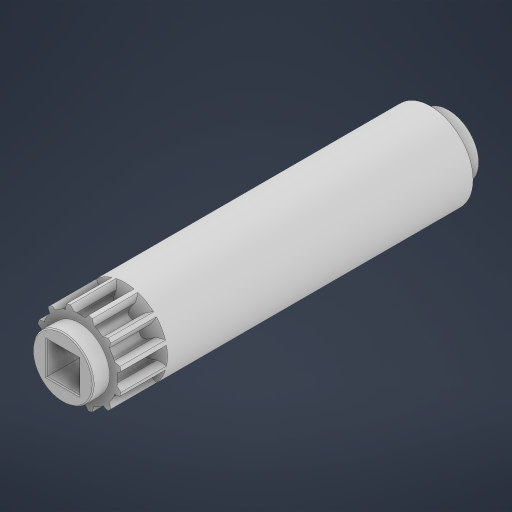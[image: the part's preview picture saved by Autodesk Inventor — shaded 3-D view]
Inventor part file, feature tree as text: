
AUTODESK INVENTOR PART (.ipt)
format: ipt  version: 2024.1 (Build 281209000, 209)  size: 670,208 bytes
history: native  units: in
note: dims shown in document units (in); Inventor stores cm internally (conversion verified against a paired STEP export)
features: extrude x10, sketch x7, projected_geometry x6, chamfer x5, reference x3, other x3, revolve x2, pattern_circular x1
ambient origin geometry x8: Origin, YZ Plane, XZ Plane, XY Plane, X Axis, Y Axis, Z Axis, Center Point
bodies: Solid1 (feature_tree)
feature tree (37):
  extrude  "Extrusion1"  TaperAngle=0.0deg  [1 undecoded]
  extrude  "Extrusion2"  Depth=4.7244in TaperAngle=360.0deg
  pattern_circular  "Circular Pattern1"  Angle=45.0deg  [1 undecoded]
  sketch  "Sketch2"  dims[d0=0.73in d1=0.0in]
  extrude  "Extrusion3"  TaperAngle=30.0deg  [1 undecoded]
  extrude  "Extrusion4"  TaperAngle=90.0deg  [1 undecoded]
  chamfer  "Chamfer1"  Angle=30.0deg  [1 undecoded]
  sketch  "Sketch3"  dims[d2=0.0in d3=0.0in d4=4.7244in d5=360.0deg]
  revolve  "Revolution1"  [1 undecoded]
  revolve  "Revolution2"  Angle=90.0deg
  extrude  "Extrusion5"  Depth=0.1675in TaperAngle=0.0deg
  extrude  "Extrusion6"  Depth=0.1675in TaperAngle=0.0deg
  chamfer  "Chamfer2"  Distance=0.3in
  sketch  "Sketch6"  dims[d9=0.16in]
  extrude  "Extrusion7"  Depth=0.1675in TaperAngle=0.0deg
  chamfer  "Chamfer3"  Distance=0.005in Angle=45.0deg
  extrude  "Extrusion8"  Depth=0.0925in TaperAngle=0.0deg
  extrude  "Extrusion9"  Depth=0.1675in TaperAngle=45.0deg
  chamfer  "Chamfer4"  Distance=0.1875in
  extrude  "Extrusion10"  Depth=0.1675in
  chamfer  "Chamfer5"  Distance=0.1675in
  projected_geometry  "Projected Loop1"
  reference  "Reference1"
  reference  "Reference2"
  reference  "Reference3"
  projected_geometry  "Projected Loop2"
  projected_geometry  "Projected Loop3"
  sketch  "Sketch4"  dims[d7=0.25in]
  sketch  "Sketch5"  dims[d8=0.16in]
  projected_geometry  "Projected Loop4"
  projected_geometry  "Projected Loop5"
  projected_geometry  "Projected Loop6"
  sketch  "Sketch7"  dims[d10=0.0825in d11=0.0in]
  sketch  "Sketch8"  dims[d12=0.1875in d13=0.0in d14=0.005in d15=0.125in d16=45.0deg d17=30.0deg d18=90.0deg d19=30.0deg d20=0.085in d21=90.0deg d22=1.0055in d23=0.0in d24=0.5051in d25=0.0in d26=0.3in d27=1.0115in d28=0.0in d29=0.005in d30=0.125in d31=45.0deg d32=0.0925in d33=0.0in d34=0.005in d35=0.125in d36=45.0deg d37=0.1875in d38=0.0in d39=0.12in d40=0.1675in d41=0.0in d42=0.005in d43=0.125in d44=45.0deg d45=0.1675in d46=0.0in d47=0.005in d48=0.125in d49=45.0deg]
  other  "<userpath>\Documents\School\FallCAD\Bio\Bio.iam"
  other  "Bio.iam"
  other  "Bio50t:1"
note: 6 required parameter values undecoded (feature->parameter linkage not recoverable at this tier; creation-order binding heuristic only, values carry confidence <= 0.55)